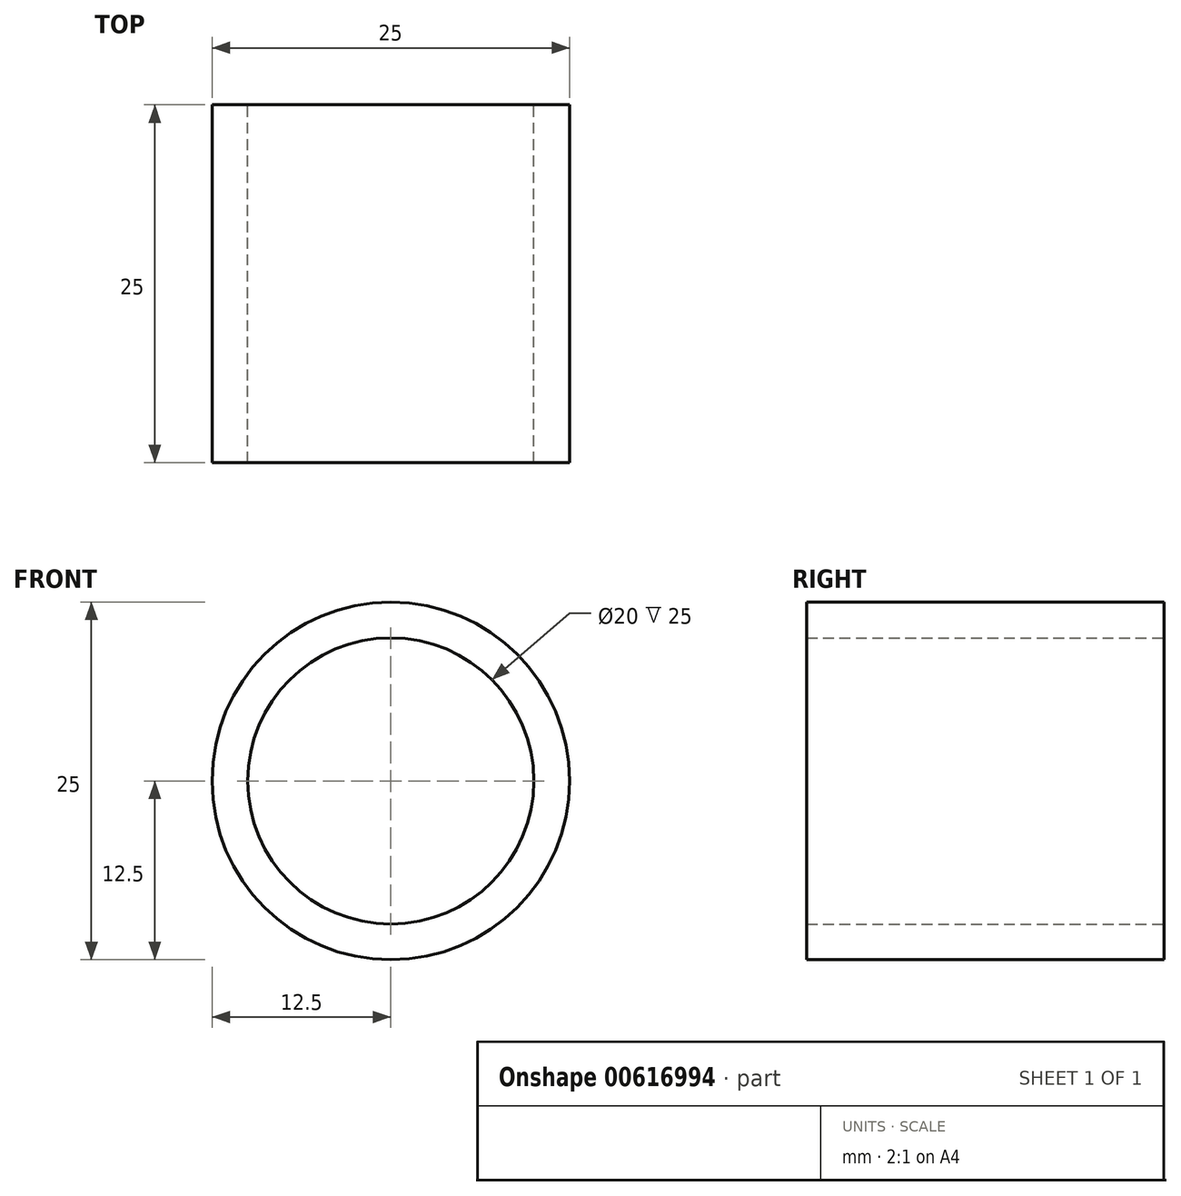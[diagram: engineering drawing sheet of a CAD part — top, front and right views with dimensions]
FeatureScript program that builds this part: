
annotation { "Feature Type Name" : "Feature", "Feature Type Description" : "" }
export const myFeature = defineFeature(function(context is Context, id is Id, definition is map)
    precondition{}
    {
        {
            var Q0;
            Q0=qCreatedBy(makeId("Front.planeOp"),FACE);
            var sketch = newSketch(context, id + "F0", { "sketchPlane" : qUnion([Q0])});
            skCircle(sketch, "E0", {"center": v(0, 0) * mm, "radius": 12.5 * mm});
            skCircle(sketch, "E1", {"center": v(0, 0) * mm, "radius": 10 * mm});
            skSolve(sketch);
        }
        {
            var Q0;
            Q0 = qSketchRegion(id + "F0", true);
            extrude(context, id + "F1", {"entities" : qUnion([Q0]), "depth" : 25 * mm, "offsetDistance" : 25 * mm});
        }
    });
